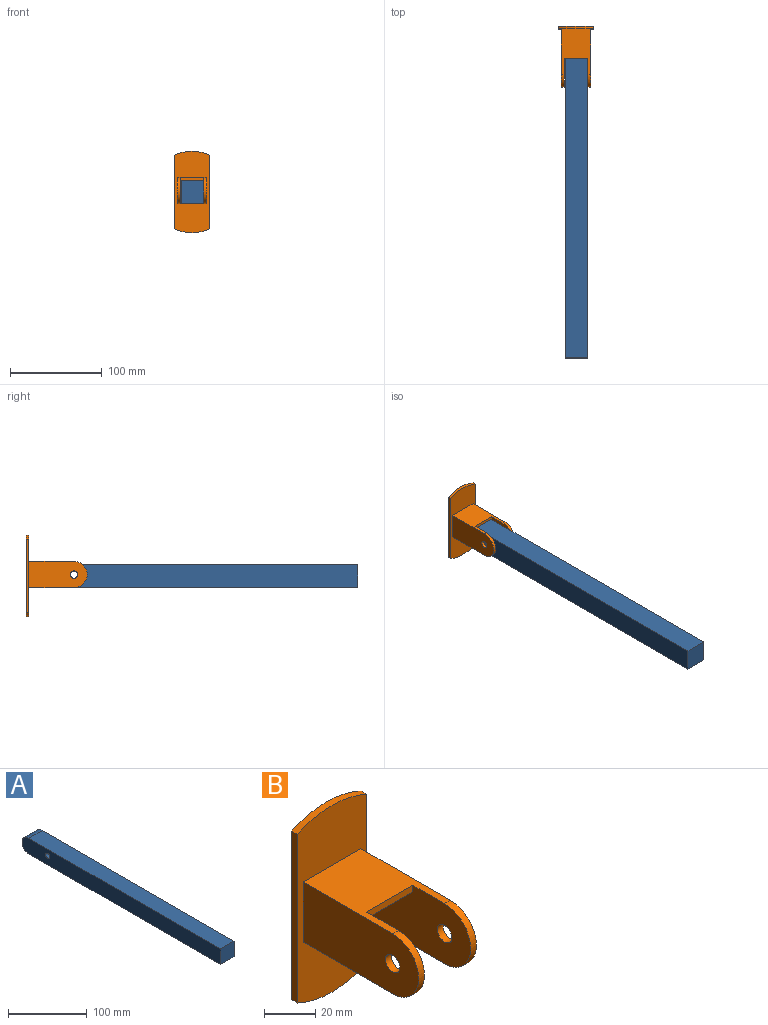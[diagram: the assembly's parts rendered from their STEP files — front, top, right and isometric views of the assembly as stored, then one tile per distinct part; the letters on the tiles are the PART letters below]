
ASSEMBLY  parts=2 mates=1
PART A: 7 faces, bbox 24.1x355.6x24.1 mm
  f0: plane 343.54x24.13mm, normal (0,0,-1), area 8289.5mm2, adj f1,f3,f4,f6
  f1: plane 355.6x24.13mm, normal (1,0,0), area 8468.7mm2, adj f0,f2,f4,f5,f6
  f2: plane 343.54x24.13mm, normal (0,0,1), area 8289.5mm2, adj f1,f3,f4,f6
  f3: plane 355.6x24.13mm, normal (-1,0,0), area 8468.7mm2, adj f0,f2,f4,f5,f6
  f4: plane 24.13x24.13mm, normal (0,-1,0), area 582.3mm2, adj f0,f1,f2,f3
  f5: cylinder r=3.97mm len=24.13mm, axis (-1,0,0), area 601.7mm2, adj f1,f3
  f6: cylinder r=12.06mm len=24.13mm, axis (1,0,0), area 914.6mm2, adj f0,f1,f2,f3
PART B: 19 faces, bbox 38.1x66.7x88.9 mm
  f0: plane 25.4x3.18mm, normal (0,-1,0), area 80.6mm2, adj f8,f11,f12,f13
  f1: plane 88.9x38.1mm, normal (0,-1,0), area 3018.2mm2, adj f2,f3,f4,f5,f7,f8,f9,f10
  f2: plane 80.32x3.18mm, normal (1,0,0), area 255mm2, adj f1,f3,f5,f6
  f3: cylinder r=44.45mm len=38.1mm, axis (0,1,0), area 125mm2, adj f1,f2,f4,f6
  f4: plane 80.32x3.18mm, normal (-1,0,0), area 255mm2, adj f1,f3,f5,f6
  f5: cylinder r=44.45mm len=38.1mm, axis (0,1,0), area 125mm2, adj f1,f2,f4,f6
  f6: plane 88.9x38.1mm, normal (0,1,0), area 3280.3mm2, adj f2,f3,f4,f5
  f7: plane 63.5x28.58mm, normal (1,0,0), area 1677.4mm2, adj f1,f8,f14,f15,f17
  f8: plane 49.21x31.75mm, normal (0,0,1), area 1118.9mm2, adj f0,f1,f7,f9,f11,f13,f15,f16
  f9: plane 63.5x28.58mm, normal (-1,0,0), area 1677.4mm2, adj f1,f8,f10,f16,f18
  f10: plane 49.21x3.18mm, normal (0,0,-1), area 156.2mm2, adj f1,f9,f11,f16
  f11: plane 63.5x28.58mm, normal (1,0,0), area 1576.6mm2, adj f0,f1,f8,f10,f12,f16,f18
  f12: plane 31.75x25.4mm, normal (0,0,-1), area 806.5mm2, adj f0,f1,f11,f13
  f13: plane 63.5x28.58mm, normal (-1,0,0), area 1576.6mm2, adj f0,f1,f8,f12,f14,f15,f17
  f14: plane 49.21x3.18mm, normal (0,0,-1), area 156.2mm2, adj f1,f7,f13,f15
  f15: cylinder r=14.29mm len=28.58mm, axis (1,0,0), area 142.5mm2, adj f7,f8,f13,f14
  f16: cylinder r=14.29mm len=28.58mm, axis (-1,0,0), area 142.5mm2, adj f8,f9,f10,f11
  f17: cylinder r=3.97mm len=7.94mm, axis (-1,0,0), area 79.2mm2, adj f7,f13
  f18: cylinder r=3.97mm len=7.94mm, axis (-1,0,0), area 79.2mm2, adj f9,f11
PLACE A rot(axis=(1,0,0),0deg) t=(0.63,0,0)mm
PLACE B at identity
MATE revolute B.f16 <-> A.f5  axis (-1,0,0) through (12.7,-52.39,1.59)mm
